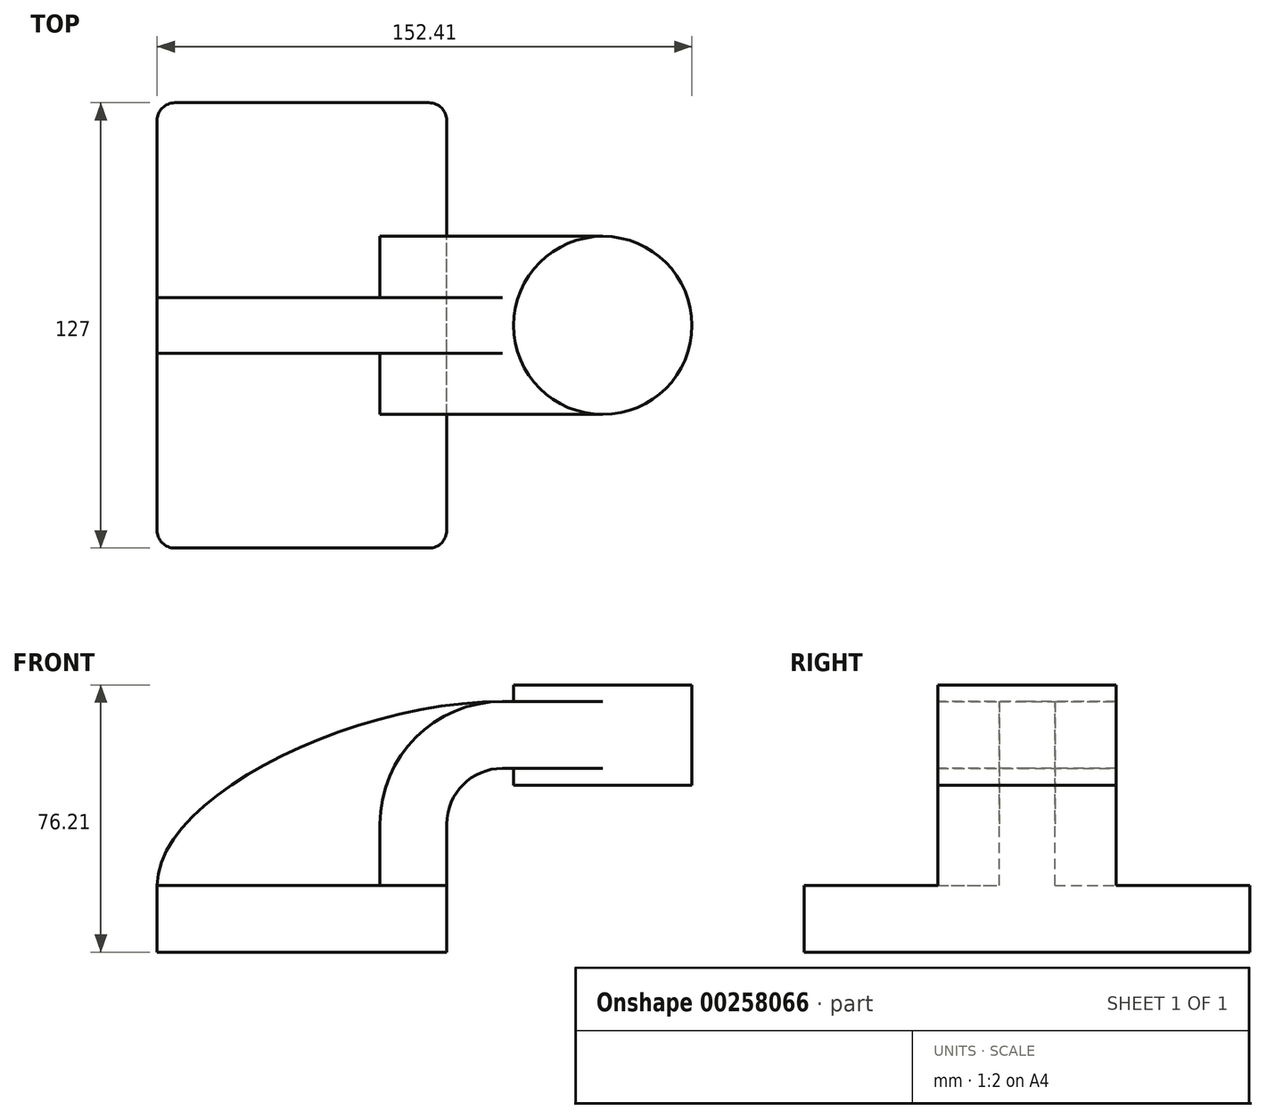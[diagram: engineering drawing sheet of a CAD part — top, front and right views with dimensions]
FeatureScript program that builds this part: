
annotation { "Feature Type Name" : "Feature", "Feature Type Description" : "" }
export const myFeature = defineFeature(function(context is Context, id is Id, definition is map)
    precondition{}
    {
        {
            var Q0;
            Q0=qCreatedBy(makeId("Front.planeOp"),FACE);
            var sketch = newSketch(context, id + "F0", { "sketchPlane" : qUnion([Q0])});
            skLineSegment(sketch, "E0.rect.bottom", {"start": v(-41.28, 9.52) * mm, "end": v(41.28, 9.52) * mm});
            skLineSegment(sketch, "E0.rect.top", {"start": v(-41.28, -9.52) * mm, "end": v(41.28, -9.52) * mm});
            skLineSegment(sketch, "E0.rect.left", {"start": v(-41.28, 9.52) * mm, "end": v(-41.28, -9.52) * mm});
            skLineSegment(sketch, "E0.rect.right", {"start": v(41.28, 9.52) * mm, "end": v(41.28, -9.52) * mm});
            skPoint(sketch, "E0.rect.middle", {"position": v(0, 0) * mm});
            skLineSegment(sketch, "E1", {"start": v(41.28, 9.52) * mm, "end": v(41.28, 27) * mm});
            skArc(sketch, "E2", {"start": v(41.28, 27) * mm, "mid": v(45.92, 38.23) * mm, "end": v(57.15, 42.88) * mm});
            skLineSegment(sketch, "E3", {"start": v(57.15, 42.88) * mm, "end": v(85.72, 42.88) * mm});
            skLineSegment(sketch, "E4.rect.bottom", {"start": v(60.32, 38.1) * mm, "end": v(111.12, 38.1) * mm});
            skLineSegment(sketch, "E4.rect.top", {"start": v(60.32, 66.68) * mm, "end": v(111.12, 66.68) * mm});
            skLineSegment(sketch, "E4.rect.left", {"start": v(60.32, 38.1) * mm, "end": v(60.32, 66.68) * mm});
            skLineSegment(sketch, "E4.rect.right", {"start": v(111.13, 38.1) * mm, "end": v(111.12, 66.68) * mm});
            skPoint(sketch, "E4.rect.middle", {"position": v(85.72, 52.39) * mm});
            skLineSegment(sketch, "E5.0", {"start": v(57.15, 61.93) * mm, "end": v(85.72, 61.93) * mm});
            skArc(sketch, "E5.1", {"start": v(22.23, 27) * mm, "mid": v(32.45, 51.7) * mm, "end": v(57.15, 61.93) * mm});
            skLineSegment(sketch, "E5.2", {"start": v(22.23, 9.52) * mm, "end": v(22.23, 27) * mm});
            skLineSegment(sketch, "E6", {"start": v(85.72, 38.1) * mm, "end": v(85.72, 66.68) * mm});
            skFitSpline(sketch, "E7", {"points": [v(-41.28, 9.52) * mm, v(57.15, 61.93) * mm], "startDerivative": vector(0, 75.32) * mm, "endDerivative": vector(129.86, 0) * mm});
            skSolve(sketch);
        }
        {
            var Q0;
            Q0=makeQuery(id+"F0.imprint","IMPRINT",FACE,{"disambiguationData":[TD([[makeQuery(id+"F0.imprint","IMPRINT",EDGE,{"derivedFrom":sQuery(id+"F0.wireOp",EDGE,"E0.rect.top")}),1.0]])]});
            extrude(context, id + "F1", {"entities" : qUnion([Q0]), "endBound" : BoundingType.SYMMETRIC, "offsetDistance" : 25.4 * mm, "depth" : 127 * mm});
        }
        {
            var Q0;
            {var subQ9=sQuery(id+"F0.wireOp",EDGE,"E1");Q0=makeQuery(id+"F0.imprint","IMPRINT",FACE,{"disambiguationData":[TD([[makeQuery(id+"F0.imprint","IMPRINT",EDGE,{"derivedFrom":subQ9}),1.0]])]});}
            var Q1;
            {var subQ0=sQuery(id+"F0.wireOp",EDGE,"E6");var subQ1=sQuery(id+"F0.wireOp",EDGE,"E3");var subQ2=makeQuery(id+"F0.imprint","INTERSECT",VERTEX,{"derivedFrom":[subQ1,subQ0]});Q1=makeQuery(id+"F0.imprint","IMPRINT",FACE,{"disambiguationData":[TD([[makeQuery(id+"F0.imprint","IMPRINT",EDGE,{"disambiguationData":[TD([[subQ2,1.0]])],"derivedFrom":subQ1}),1.0]])]});}
            extrude(context, id + "F2", {"entities" : qUnion([Q0, Q1]), "operationType" : NewBodyOperationType.ADD, "endBound" : BoundingType.SYMMETRIC, "offsetDistance" : 25.4 * mm, "depth" : 50.8 * mm});
        }
        {
            var Q0;
            {var subQ3=sQuery(id+"F0.wireOp",EDGE,"E5.2");Q0=makeQuery(id+"F0.imprint","IMPRINT",FACE,{"disambiguationData":[TD([[makeQuery(id+"F0.imprint","IMPRINT",EDGE,{"derivedFrom":subQ3}),1.0]])]});}
            extrude(context, id + "F3", {"entities" : qUnion([Q0]), "operationType" : NewBodyOperationType.ADD, "endBound" : BoundingType.SYMMETRIC, "offsetDistance" : 25.4 * mm, "depth" : 15.88 * mm});
        }
        {
            var Q0;
            {var subQ5=sQuery(id+"F0.wireOp",EDGE,"E4.rect.right");Q0=makeQuery(id+"F0.imprint","IMPRINT",FACE,{"disambiguationData":[TD([[makeQuery(id+"F0.imprint","IMPRINT",EDGE,{"derivedFrom":subQ5}),1.0]])]});}
            var Q1;
            Q1=sQuery(id+"F0.wireOp",EDGE,"E6");
            revolve(context, id + "F4", {"operationType" : NewBodyOperationType.ADD, "surfaceOperationType" : NewSurfaceOperationType.NEW, "entities" : qUnion([Q0]), "axis" : qUnion([Q1]), "revolveType" : RevolveType.FULL});
        }
        {
            var Q0;
            Q0=makeQuery(id+"F1.opExtrude","CAP_EDGE",EDGE,{"disambiguationData":[OSD([sQuery(id+"F0.wireOp",EDGE,"E0.rect.right")])],"isStart":false});
            var Q1;
            Q1=makeQuery(id+"F1.opExtrude","CAP_EDGE",EDGE,{"disambiguationData":[OSD([sQuery(id+"F0.wireOp",EDGE,"E0.rect.left")])],"isStart":false});
            var Q2;
            Q2=makeQuery(id+"F1.opExtrude","CAP_EDGE",EDGE,{"disambiguationData":[OSD([sQuery(id+"F0.wireOp",EDGE,"E0.rect.right")])],"isStart":true});
            var Q3;
            Q3=makeQuery(id+"F1.opExtrude","CAP_EDGE",EDGE,{"disambiguationData":[OSD([sQuery(id+"F0.wireOp",EDGE,"E0.rect.left")])],"isStart":true});
            fillet(context, id + "F5", {"entities" : qUnion([Q0, Q1, Q2, Q3]), "radius" : 5.08 * mm, "tangentPropagation" : true, "defaultsChanged" : false, "vertexSettings" : [], "allowEdgeOverflow" : false});
        }
    });
